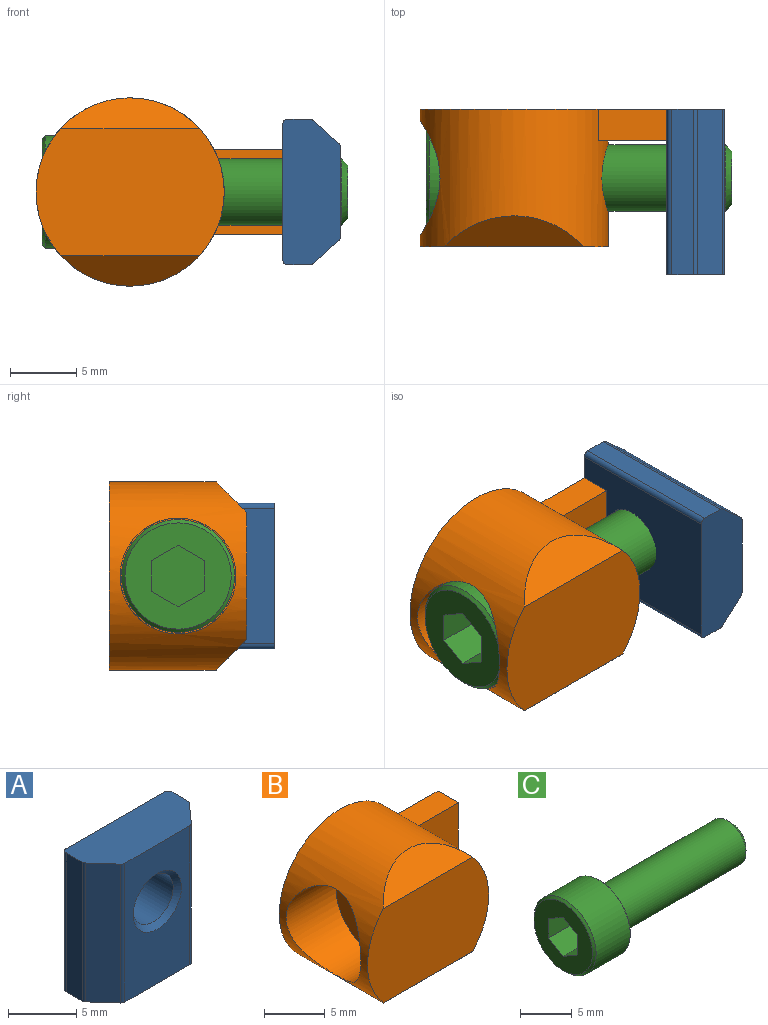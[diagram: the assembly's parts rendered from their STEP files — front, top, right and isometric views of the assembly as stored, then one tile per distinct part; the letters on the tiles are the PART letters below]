
ASSEMBLY  parts=3 mates=2
PART A: 17 faces, bbox 10.9x4.3x12.4 mm
  f0: cylinder r=0.38mm len=12.45mm, axis (0,0,-1), area 7.4mm2, adj f1,f11,f12,f13
  f1: plane 12.45x1.65mm, normal (-1,0,0), area 20.5mm2, adj f0,f2,f12,f13
  f2: cylinder r=0.38mm len=12.45mm, axis (0,0,-1), area 3.5mm2, adj f1,f3,f12,f13
  f3: plane 12.45x1.94mm, normal (-0.75,-0.67,0), area 32.3mm2, adj f2,f4,f12,f13
  f4: cylinder r=0.38mm len=12.45mm, axis (0,0,-1), area 4mm2, adj f3,f5,f12,f13
  f5: plane 12.45x6.72mm, normal (0,-1,0), area 64mm2, adj f4,f6,f12,f13,f16
  f6: cylinder r=0.38mm len=12.45mm, axis (0,0,-1), area 4mm2, adj f5,f7,f12,f13
  f7: plane 12.45x1.94mm, normal (0.75,-0.67,0), area 32.3mm2, adj f6,f8,f12,f13
  f8: cylinder r=0.38mm len=12.45mm, axis (0,0,-1), area 3.5mm2, adj f7,f9,f12,f13
  f9: plane 12.45x1.65mm, normal (1,0,0), area 20.5mm2, adj f8,f10,f12,f13
  f10: cylinder r=0.38mm len=12.45mm, axis (0,0,-1), area 7.4mm2, adj f9,f11,f12,f13
  f11: plane 12.45x10.19mm, normal (0,1,0), area 107.1mm2, adj f0,f10,f12,f13,f14
  f12: plane 10.95x4.34mm, normal (0,0,1), area 43.3mm2, adj f0,f1,f2,f3,f4,f5,f6,f7
  f13: plane 10.95x4.34mm, normal (0,0,-1), area 43.3mm2, adj f0,f1,f2,f3,f4,f5,f6,f7
  f14: cone r=2.5mm half-angle=45deg, axis (0,1,0), area 8.8mm2, adj f11,f15
  f15: cylinder r=2.07mm len=4.13mm, axis (0,-1,0), area 45.2mm2, adj f14,f16
  f16: cone r=2.07mm half-angle=45deg, axis (0,-1,0), area 8.8mm2, adj f5,f15
PART B: 12 faces, bbox 18.5x10.3x14.2 mm
  f0: cylinder r=7.07mm len=14.15mm, axis (0,-1,0), area 323.1mm2, adj f1,f2,f3,f4,f5,f7,f8,f9
  f1: plane 14.15x9.55mm, normal (0,-1,0), area 124mm2, adj f0,f7,f8
  f2: plane 18.55x14.15mm, normal (0,1,0), area 186.7mm2, adj f0,f3,f4,f6
  f3: plane 5.15x2.36mm, normal (0,0,1), area 12.2mm2, adj f0,f2,f5,f6
  f4: plane 5.15x2.36mm, normal (0,0,-1), area 12.2mm2, adj f0,f2,f5,f6
  f5: plane 6.35x5.15mm, normal (0,-1,0), area 29.5mm2, adj f0,f3,f4,f6
  f6: plane 6.35x2.36mm, normal (1,0,0), area 15mm2, adj f2,f3,f4,f5
  f7: plane 10.44x2.3mm, normal (0,-0.71,-0.71), area 23.5mm2, adj f0,f1
  f8: plane 10.44x2.3mm, normal (0,-0.71,0.71), area 23.5mm2, adj f0,f1
  f9: cylinder r=2.57mm len=8.31mm, axis (1,0,0), area 130.4mm2, adj f0,f11
  f10: cylinder r=4.36mm len=8.71mm, axis (1,0,0), area 140mm2, adj f0,f11
  f11: plane 8.71x8.71mm, normal (-1,0,0), area 38.8mm2, adj f9,f10
PART C: 15 faces, bbox 23x8.5x8.5 mm
  f0: plane 7.99x7.99mm, normal (-1,0,0), area 36.3mm2, adj f1,f8,f9,f10,f11,f12,f13
  f1: cone r=4mm half-angle=45deg, axis (1,0,0), area 9.3mm2, adj f0,f2
  f2: cylinder r=4.25mm len=8.5mm, axis (1,0,0), area 124.4mm2, adj f1,f3
  f3: cone r=4.25mm half-angle=45deg, axis (-1,0,0), area 3.2mm2, adj f2,f4
  f4: plane 8.33x8.33mm, normal (1,0,0), area 34.9mm2, adj f3,f5
  f5: cylinder r=2.5mm len=17.51mm, axis (1,0,0), area 275mm2, adj f4,f6
  f6: cone r=2.5mm half-angle=45deg, axis (-1,0,0), area 9.8mm2, adj f5,f7
  f7: plane 4.02x4.02mm, normal (1,0,0), area 12.7mm2, adj f6
  f8: plane 4x2mm, normal (0,-0.5,-0.87), area 9.2mm2, adj f0,f9,f13,f14
  f9: plane 4x2mm, normal (0,0.5,-0.87), area 9.2mm2, adj f0,f8,f10,f14
  f10: plane 4x2.31mm, normal (0,1,0), area 9.2mm2, adj f0,f9,f11,f14
  f11: plane 4x2mm, normal (0,0.5,0.87), area 9.2mm2, adj f0,f10,f12,f14
  f12: plane 4x2mm, normal (0,-0.5,0.87), area 9.2mm2, adj f0,f11,f13,f14
  f13: plane 4x2.31mm, normal (0,-1,0), area 9.2mm2, adj f0,f8,f12,f14
  f14: plane 4.62x4mm, normal (-1,0,0), area 13.9mm2, adj f8,f9,f10,f11,f12,f13
PLACE A rot(axis=(-0.58,0.58,0.58),120deg) t=(14.67,4.4,2.12)mm
PLACE B t=(-1.14,-0.86,2.12)mm
PLACE C t=(-2.76,4.3,2.12)mm
MATE fastened A.f11 <-> B.f6  axis (-1,0,0) through (10.33,8.48,2.12)mm
MATE fastened C.f1 <-> B.f9  axis (1,0,0) through (5.99,4.3,2.12)mm
